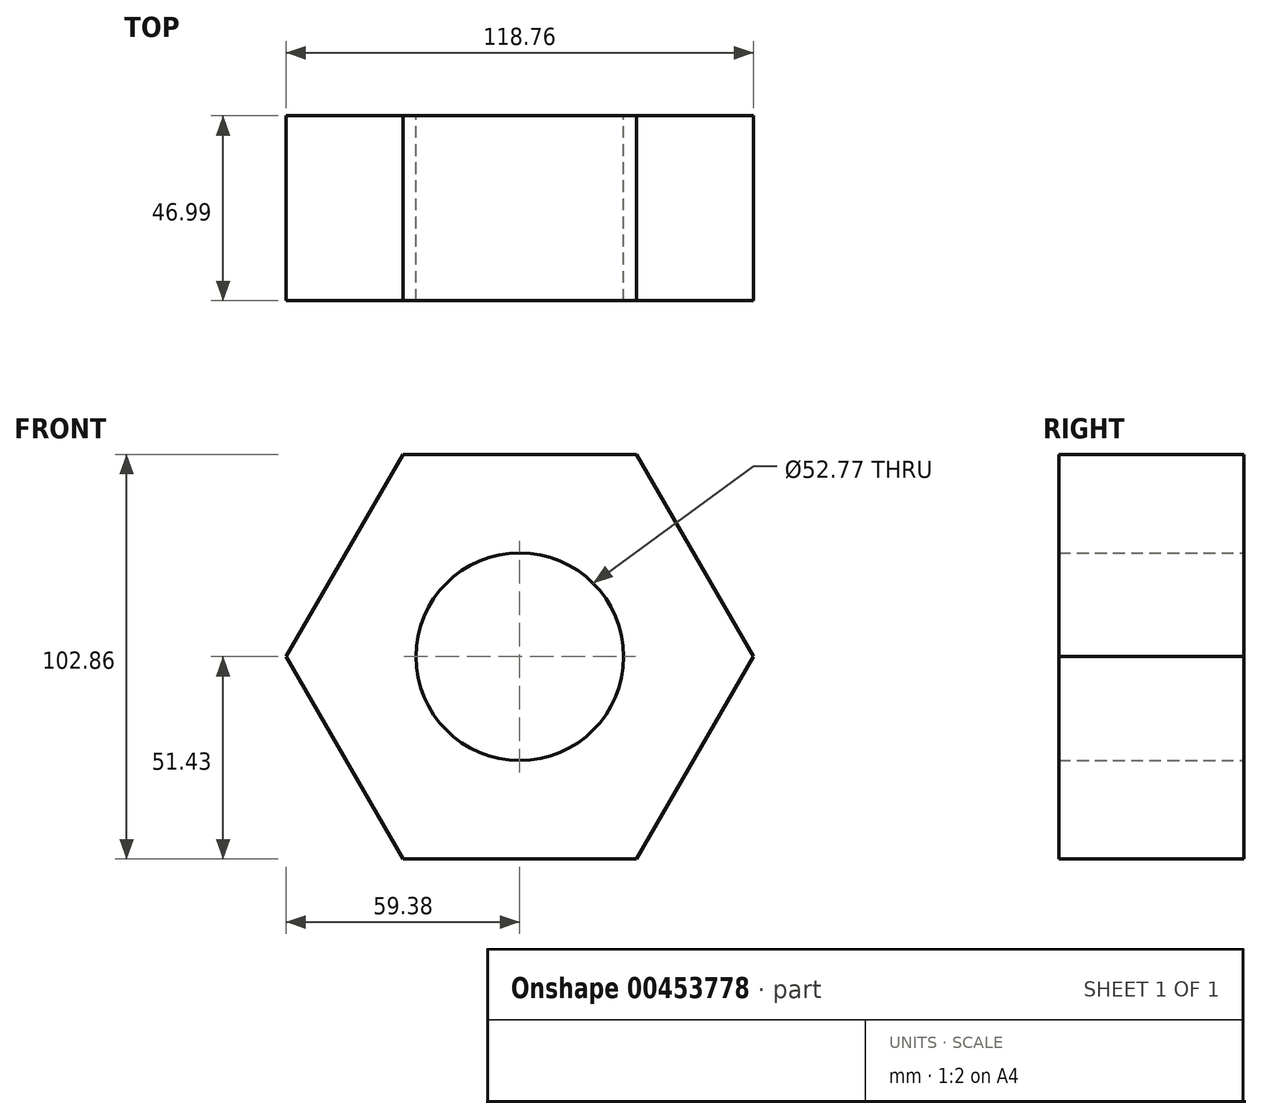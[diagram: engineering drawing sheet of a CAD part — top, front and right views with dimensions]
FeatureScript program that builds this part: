
annotation { "Feature Type Name" : "Feature", "Feature Type Description" : "" }
export const myFeature = defineFeature(function(context is Context, id is Id, definition is map)
    precondition{}
    {
        {
            var Q0;
            Q0=qCreatedBy(makeId("Front.planeOp"),FACE);
            var sketch = newSketch(context, id + "F0", { "sketchPlane" : qUnion([Q0])});
            skCircle(sketch, "E0.cCircle", {"center": v(0, 0) * mm, "radius": 51.43 * mm, "construction": true});
            skLineSegment(sketch, "E0.0", {"start": v(29.7, -51.43) * mm, "end": v(-29.7, -51.43) * mm});
            skLineSegment(sketch, "E0.1", {"start": v(-29.7, -51.43) * mm, "end": v(-59.38, 0) * mm});
            skLineSegment(sketch, "E0.2", {"start": v(-59.38, 0) * mm, "end": v(-29.7, 51.43) * mm});
            skLineSegment(sketch, "E0.3", {"start": v(-29.7, 51.43) * mm, "end": v(29.7, 51.43) * mm});
            skLineSegment(sketch, "E0.4", {"start": v(29.7, 51.43) * mm, "end": v(59.38, 0) * mm});
            skLineSegment(sketch, "E0.5", {"start": v(59.38, 0) * mm, "end": v(29.7, -51.43) * mm});
            skPoint(sketch, "E0.0.midPoint", {"position": v(0, -51.43) * mm});
            skSolve(sketch);
        }
        {
            var Q0;
            Q0 = qSketchRegion(id + "F0", true);
            extrude(context, id + "F1", {"entities" : qUnion([Q0]), "oppositeDirection" : true, "depth" : 47 * mm});
        }
        {
            var Q0;
            Q0=makeQuery(id+"F1.opExtrude","CAP_FACE",FACE,{"disambiguationData":[OSD([sQuery(id+"F0.wireOp",EDGE,"E0.0"),sQuery(id+"F0.wireOp",EDGE,"E0.1"),sQuery(id+"F0.wireOp",EDGE,"E0.2"),sQuery(id+"F0.wireOp",EDGE,"E0.3"),sQuery(id+"F0.wireOp",EDGE,"E0.4"),sQuery(id+"F0.wireOp",EDGE,"E0.5")])],"isStart":false});
            var sketch = newSketch(context, id + "F2", { "sketchPlane" : qUnion([Q0])});
            skCircle(sketch, "E1", {"center": v(0, 0) * mm, "radius": 26.39 * mm});
            skSolve(sketch);
        }
        {
            var Q0;
            Q0 = qSketchRegion(id + "F2", true);
            extrude(context, id + "F3", {"entities" : qUnion([Q0]), "operationType" : NewBodyOperationType.REMOVE, "endBound" : BoundingType.THROUGH_ALL, "oppositeDirection" : true, "depth" : 25.4 * mm});
        }
    });
